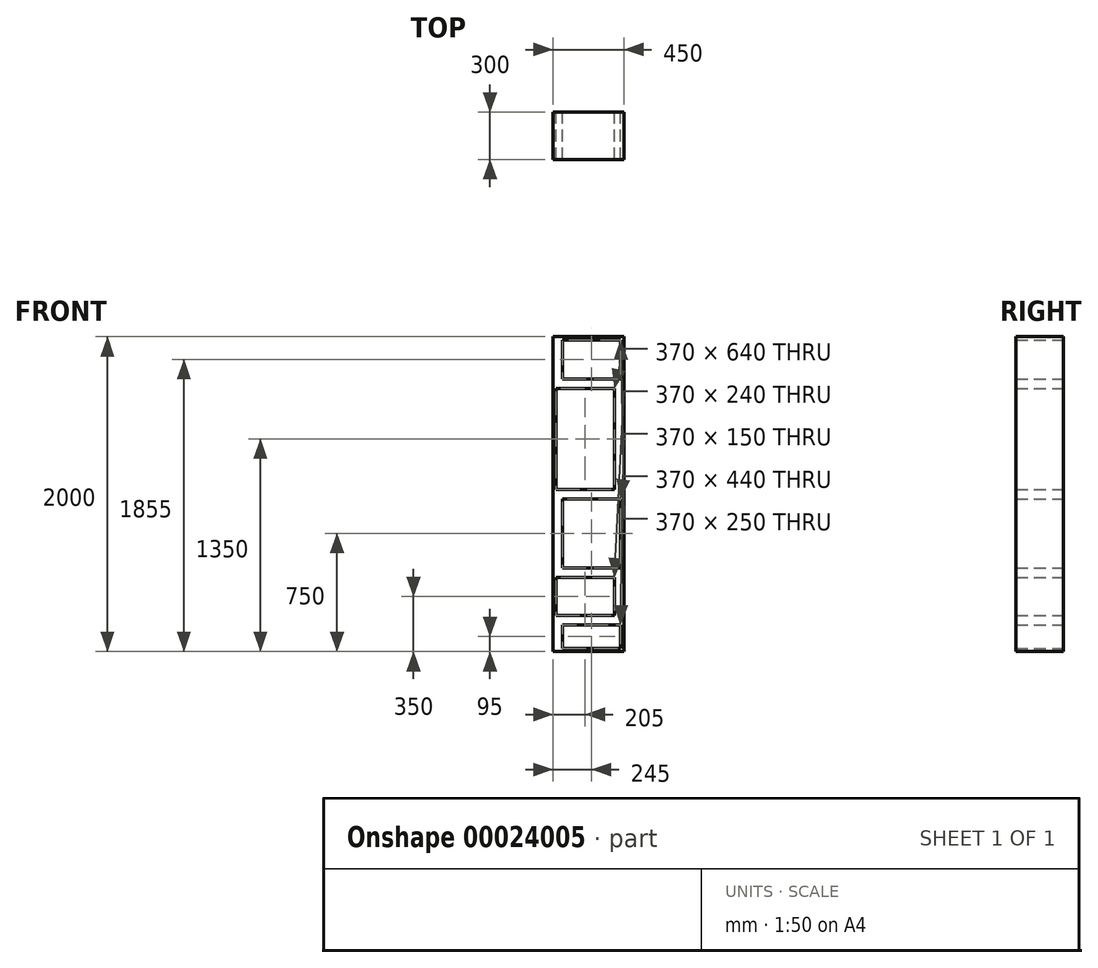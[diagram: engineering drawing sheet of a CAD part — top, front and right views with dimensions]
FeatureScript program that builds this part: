
annotation { "Feature Type Name" : "Feature", "Feature Type Description" : "" }
export const myFeature = defineFeature(function(context is Context, id is Id, definition is map)
    precondition{}
    {
        {
            var Q0;
            Q0=qCreatedBy(makeId("Front.planeOp"),FACE);
            var sketch = newSketch(context, id + "F0", { "sketchPlane" : qUnion([Q0])});
            skLineSegment(sketch, "E0.bottom", {"start": v(-1686.27, 784.55) * mm, "end": v(-1656.27, 784.55) * mm});
            skLineSegment(sketch, "E0.top", {"start": v(-1686.27, -1215.45) * mm, "end": v(-1656.27, -1215.45) * mm});
            skLineSegment(sketch, "E0.left", {"start": v(-1686.27, 784.55) * mm, "end": v(-1686.27, -215.45) * mm});
            skLineSegment(sketch, "E0.right", {"start": v(-1236.27, 784.55) * mm, "end": v(-1236.27, 484.55) * mm});
            skLineSegment(sketch, "E1.bottom", {"start": v(-1656.27, 784.55) * mm, "end": v(-1266.27, 784.55) * mm});
            skLineSegment(sketch, "E1.top", {"start": v(-1656.27, -1215.45) * mm, "end": v(-1266.27, -1215.45) * mm});
            skLineSegment(sketch, "E1.left", {"start": v(-1656.27, 784.55) * mm, "end": v(-1656.27, 484.55) * mm, "construction": true});
            skLineSegment(sketch, "E1.right", {"start": v(-1266.27, 784.55) * mm, "end": v(-1266.27, 484.55) * mm, "construction": true});
            skLineSegment(sketch, "E2.bottom", {"start": v(-1686.27, 484.55) * mm, "end": v(-1656.27, 484.55) * mm, "construction": true});
            skLineSegment(sketch, "E2.top", {"start": v(-1686.27, -215.45) * mm, "end": v(-1656.27, -215.45) * mm, "construction": true});
            skLineSegment(sketch, "E2.left", {"start": v(-1686.27, 484.55) * mm, "end": v(-1686.27, 484.55) * mm});
            skLineSegment(sketch, "E2.right", {"start": v(-1236.27, 484.55) * mm, "end": v(-1236.27, 484.55) * mm});
            skLineSegment(sketch, "E3.bottom", {"start": v(-1686.27, -715.45) * mm, "end": v(-1656.27, -715.45) * mm, "construction": true});
            skLineSegment(sketch, "E3.top", {"start": v(-1686.27, -1015.45) * mm, "end": v(-1656.27, -1015.45) * mm, "construction": true});
            skLineSegment(sketch, "E3.left", {"start": v(-1686.27, -715.45) * mm, "end": v(-1686.27, -715.45) * mm});
            skLineSegment(sketch, "E3.right", {"start": v(-1236.27, -715.45) * mm, "end": v(-1236.27, -715.45) * mm});
            skLineSegment(sketch, "E4", {"start": v(-1656.27, 484.55) * mm, "end": v(-1656.27, -215.45) * mm, "construction": true});
            skLineSegment(sketch, "E5", {"start": v(-1266.27, 484.55) * mm, "end": v(-1236.27, 484.55) * mm, "construction": true});
            skLineSegment(sketch, "E6", {"start": v(-1266.27, 484.55) * mm, "end": v(-1266.27, -215.45) * mm, "construction": true});
            skLineSegment(sketch, "E7", {"start": v(-1266.27, -215.45) * mm, "end": v(-1266.27, -715.45) * mm, "construction": true});
            skLineSegment(sketch, "E8", {"start": v(-1266.27, -715.45) * mm, "end": v(-1266.27, -1015.45) * mm, "construction": true});
            skLineSegment(sketch, "E9", {"start": v(-1266.27, -1015.45) * mm, "end": v(-1266.27, -1215.45) * mm, "construction": true});
            skLineSegment(sketch, "E10", {"start": v(-1656.27, -1015.45) * mm, "end": v(-1656.27, -1215.45) * mm, "construction": true});
            skLineSegment(sketch, "E11", {"start": v(-1656.27, -715.45) * mm, "end": v(-1656.27, -1015.45) * mm, "construction": true});
            skLineSegment(sketch, "E12", {"start": v(-1656.27, -215.45) * mm, "end": v(-1656.27, -715.45) * mm, "construction": true});
            skLineSegment(sketch, "E13", {"start": v(-1656.27, 484.55) * mm, "end": v(-1266.27, 484.55) * mm, "construction": true});
            skLineSegment(sketch, "E14", {"start": v(-1656.27, -215.45) * mm, "end": v(-1266.27, -215.45) * mm, "construction": true});
            skLineSegment(sketch, "E15", {"start": v(-1266.27, -215.45) * mm, "end": v(-1236.27, -215.45) * mm, "construction": true});
            skLineSegment(sketch, "E16", {"start": v(-1266.27, -715.45) * mm, "end": v(-1236.27, -715.45) * mm, "construction": true});
            skLineSegment(sketch, "E17", {"start": v(-1266.27, -1015.45) * mm, "end": v(-1236.27, -1015.45) * mm, "construction": true});
            skLineSegment(sketch, "E18", {"start": v(-1656.27, -1015.45) * mm, "end": v(-1266.27, -1015.45) * mm, "construction": true});
            skLineSegment(sketch, "E19", {"start": v(-1656.27, -715.45) * mm, "end": v(-1266.27, -715.45) * mm, "construction": true});
            skLineSegment(sketch, "E20", {"start": v(-1686.27, -1015.45) * mm, "end": v(-1686.27, -1215.45) * mm});
            skLineSegment(sketch, "E21", {"start": v(-1686.27, -715.45) * mm, "end": v(-1686.27, -1015.45) * mm});
            skLineSegment(sketch, "E22", {"start": v(-1686.27, -215.45) * mm, "end": v(-1686.27, -1015.45) * mm});
            skLineSegment(sketch, "E23", {"start": v(-1686.27, 484.55) * mm, "end": v(-1686.27, -215.45) * mm});
            skLineSegment(sketch, "E24", {"start": v(-1266.27, 784.55) * mm, "end": v(-1236.27, 784.55) * mm});
            skLineSegment(sketch, "E25", {"start": v(-1266.27, -1215.45) * mm, "end": v(-1236.27, -1215.45) * mm});
            skLineSegment(sketch, "E26", {"start": v(-1236.27, -1015.45) * mm, "end": v(-1236.27, -1215.45) * mm});
            skLineSegment(sketch, "E27", {"start": v(-1236.27, -715.45) * mm, "end": v(-1236.27, -1015.45) * mm});
            skLineSegment(sketch, "E28", {"start": v(-1236.27, -215.45) * mm, "end": v(-1236.27, -1015.45) * mm});
            skLineSegment(sketch, "E29", {"start": v(-1236.27, 484.55) * mm, "end": v(-1236.27, -215.45) * mm});
            skSolve(sketch);
        }
        {
            var Q0;
            Q0=qCreatedBy(makeId("Front.planeOp"),FACE);
            var sketch = newSketch(context, id + "F1", { "sketchPlane" : qUnion([Q0])});
            skLineSegment(sketch, "E30.0", {"start": v(-1646.27, -1025.45) * mm, "end": v(-1646.27, -1215.45) * mm});
            skLineSegment(sketch, "E30.1", {"start": v(-1646.27, -1025.45) * mm, "end": v(-1256.27, -1025.45) * mm});
            skLineSegment(sketch, "E30.2", {"start": v(-1256.27, -705.45) * mm, "end": v(-1256.27, -1025.45) * mm});
            skLineSegment(sketch, "E30.3", {"start": v(-1646.27, -705.45) * mm, "end": v(-1256.27, -705.45) * mm});
            skLineSegment(sketch, "E30.4", {"start": v(-1646.27, -225.45) * mm, "end": v(-1646.27, -705.45) * mm});
            skLineSegment(sketch, "E30.5", {"start": v(-1646.27, -225.45) * mm, "end": v(-1256.27, -225.45) * mm});
            skLineSegment(sketch, "E30.6", {"start": v(-1256.27, 494.55) * mm, "end": v(-1256.27, -225.45) * mm});
            skLineSegment(sketch, "E30.7", {"start": v(-1646.27, 494.55) * mm, "end": v(-1256.27, 494.55) * mm});
            skLineSegment(sketch, "E30.8", {"start": v(-1646.27, 784.55) * mm, "end": v(-1646.27, 494.55) * mm});
            skLineSegment(sketch, "E31.0", {"start": v(-1666.27, -1005.45) * mm, "end": v(-1666.27, -1215.45) * mm});
            skLineSegment(sketch, "E31.1", {"start": v(-1666.27, -1005.45) * mm, "end": v(-1276.27, -1005.45) * mm});
            skLineSegment(sketch, "E31.2", {"start": v(-1276.27, -725.45) * mm, "end": v(-1276.27, -1005.45) * mm});
            skLineSegment(sketch, "E31.3", {"start": v(-1666.27, -725.45) * mm, "end": v(-1276.27, -725.45) * mm});
            skLineSegment(sketch, "E31.4", {"start": v(-1666.27, -205.45) * mm, "end": v(-1666.27, -725.45) * mm});
            skLineSegment(sketch, "E31.5", {"start": v(-1666.27, -205.45) * mm, "end": v(-1276.27, -205.45) * mm});
            skLineSegment(sketch, "E31.6", {"start": v(-1276.27, 474.55) * mm, "end": v(-1276.27, -205.45) * mm});
            skLineSegment(sketch, "E31.7", {"start": v(-1666.27, 474.55) * mm, "end": v(-1276.27, 474.55) * mm});
            skLineSegment(sketch, "E31.8", {"start": v(-1666.27, 784.55) * mm, "end": v(-1666.27, 474.55) * mm});
            skLineSegment(sketch, "E32", {"start": v(-1646.27, -1215.45) * mm, "end": v(-1666.27, -1215.45) * mm});
            skLineSegment(sketch, "E33", {"start": v(-1666.27, 784.55) * mm, "end": v(-1646.27, 784.55) * mm});
            skSolve(sketch);
        }
        {
            var Q0;
            Q0=qCreatedBy(makeId("Front.planeOp"),FACE);
            var sketch = newSketch(context, id + "F2", { "sketchPlane" : qUnion([Q0])});
            skLineSegment(sketch, "E34.bottom", {"start": v(-1686.27, 474.55) * mm, "end": v(-1276.27, 474.55) * mm});
            skLineSegment(sketch, "E34.top", {"start": v(-1686.27, -205.45) * mm, "end": v(-1276.27, -205.45) * mm});
            skLineSegment(sketch, "E34.left", {"start": v(-1686.27, 474.55) * mm, "end": v(-1686.27, -205.45) * mm});
            skLineSegment(sketch, "E34.right", {"start": v(-1276.27, 474.55) * mm, "end": v(-1276.27, -205.45) * mm});
            skLineSegment(sketch, "E35.bottom", {"start": v(-1686.27, -725.45) * mm, "end": v(-1276.27, -725.45) * mm});
            skLineSegment(sketch, "E35.top", {"start": v(-1686.27, -1005.45) * mm, "end": v(-1276.27, -1005.45) * mm});
            skLineSegment(sketch, "E35.left", {"start": v(-1686.27, -725.45) * mm, "end": v(-1686.27, -1005.45) * mm});
            skLineSegment(sketch, "E35.right", {"start": v(-1276.27, -725.45) * mm, "end": v(-1276.27, -1005.45) * mm});
            skLineSegment(sketch, "E36.0", {"start": v(-1666.27, -745.45) * mm, "end": v(-1296.27, -745.45) * mm});
            skLineSegment(sketch, "E36.1", {"start": v(-1666.27, -745.45) * mm, "end": v(-1666.27, -985.45) * mm});
            skLineSegment(sketch, "E36.2", {"start": v(-1666.27, -985.45) * mm, "end": v(-1296.27, -985.45) * mm});
            skLineSegment(sketch, "E36.3", {"start": v(-1296.27, -745.45) * mm, "end": v(-1296.27, -985.45) * mm});
            skLineSegment(sketch, "E37.bottom", {"start": v(-1646.27, -1025.45) * mm, "end": v(-1236.27, -1025.45) * mm});
            skLineSegment(sketch, "E37.top", {"start": v(-1646.27, -1215.45) * mm, "end": v(-1236.27, -1215.45) * mm});
            skLineSegment(sketch, "E37.left", {"start": v(-1646.27, -1025.45) * mm, "end": v(-1646.27, -1215.45) * mm});
            skLineSegment(sketch, "E37.right", {"start": v(-1236.27, -1025.45) * mm, "end": v(-1236.27, -1215.45) * mm});
            skLineSegment(sketch, "E38.bottom", {"start": v(-1646.27, -225.45) * mm, "end": v(-1236.27, -225.45) * mm});
            skLineSegment(sketch, "E38.top", {"start": v(-1646.27, -705.45) * mm, "end": v(-1236.27, -705.45) * mm});
            skLineSegment(sketch, "E38.left", {"start": v(-1646.27, -225.45) * mm, "end": v(-1646.27, -705.45) * mm});
            skLineSegment(sketch, "E38.right", {"start": v(-1236.27, -225.45) * mm, "end": v(-1236.27, -705.45) * mm});
            skLineSegment(sketch, "E39.bottom", {"start": v(-1646.27, 494.55) * mm, "end": v(-1236.27, 494.55) * mm});
            skLineSegment(sketch, "E39.top", {"start": v(-1646.27, 784.55) * mm, "end": v(-1236.27, 784.55) * mm});
            skLineSegment(sketch, "E39.left", {"start": v(-1646.27, 494.55) * mm, "end": v(-1646.27, 784.55) * mm});
            skLineSegment(sketch, "E39.right", {"start": v(-1236.27, 494.55) * mm, "end": v(-1236.27, 784.55) * mm});
            skLineSegment(sketch, "E40.0", {"start": v(-1626.27, -245.45) * mm, "end": v(-1256.27, -245.45) * mm});
            skLineSegment(sketch, "E40.1", {"start": v(-1626.27, -245.45) * mm, "end": v(-1626.27, -685.45) * mm});
            skLineSegment(sketch, "E40.2", {"start": v(-1626.27, -685.45) * mm, "end": v(-1256.27, -685.45) * mm});
            skLineSegment(sketch, "E40.3", {"start": v(-1256.27, -245.45) * mm, "end": v(-1256.27, -685.45) * mm});
            skLineSegment(sketch, "E41.0", {"start": v(-1666.27, 454.55) * mm, "end": v(-1666.27, -185.45) * mm});
            skLineSegment(sketch, "E41.1", {"start": v(-1666.27, 454.55) * mm, "end": v(-1296.27, 454.55) * mm});
            skLineSegment(sketch, "E41.2", {"start": v(-1296.27, 454.55) * mm, "end": v(-1296.27, -185.45) * mm});
            skLineSegment(sketch, "E41.3", {"start": v(-1666.27, -185.45) * mm, "end": v(-1296.27, -185.45) * mm});
            skLineSegment(sketch, "E42.0", {"start": v(-1626.27, -1045.45) * mm, "end": v(-1626.27, -1195.45) * mm});
            skLineSegment(sketch, "E42.1", {"start": v(-1626.27, -1045.45) * mm, "end": v(-1256.27, -1045.45) * mm});
            skLineSegment(sketch, "E42.2", {"start": v(-1256.27, -1045.45) * mm, "end": v(-1256.27, -1195.45) * mm});
            skLineSegment(sketch, "E42.3", {"start": v(-1626.27, -1195.45) * mm, "end": v(-1256.27, -1195.45) * mm});
            skLineSegment(sketch, "E43.0", {"start": v(-1256.27, 514.55) * mm, "end": v(-1256.27, 764.55) * mm});
            skLineSegment(sketch, "E43.1", {"start": v(-1626.27, 514.55) * mm, "end": v(-1256.27, 514.55) * mm});
            skLineSegment(sketch, "E43.2", {"start": v(-1626.27, 514.55) * mm, "end": v(-1626.27, 764.55) * mm});
            skLineSegment(sketch, "E43.3", {"start": v(-1626.27, 764.55) * mm, "end": v(-1256.27, 764.55) * mm});
            skSolve(sketch);
        }
        {
            var Q0;
            Q0=qCreatedBy(makeId("Front.planeOp"),FACE);
            var sketch = newSketch(context, id + "F3", { "sketchPlane" : qUnion([Q0])});
            skLineSegment(sketch, "E44.bottom", {"start": v(-1686.27, 784.55) * mm, "end": v(-1236.27, 784.55) * mm, "construction": true});
            skLineSegment(sketch, "E44.top", {"start": v(-1686.27, -1215.45) * mm, "end": v(-1236.27, -1215.45) * mm, "construction": true});
            skLineSegment(sketch, "E44.left", {"start": v(-1686.27, 784.55) * mm, "end": v(-1686.27, -1215.45) * mm});
            skLineSegment(sketch, "E44.right", {"start": v(-1236.27, 784.55) * mm, "end": v(-1236.27, -1215.45) * mm});
            skLineSegment(sketch, "E45.0", {"start": v(-1666.27, 784.55) * mm, "end": v(-1666.27, -1215.45) * mm});
            skLineSegment(sketch, "E46.0", {"start": v(-1256.27, 784.55) * mm, "end": v(-1256.27, -1215.45) * mm});
            skLineSegment(sketch, "E47.bottom", {"start": v(-1686.27, 784.55) * mm, "end": v(-1666.27, 784.55) * mm});
            skLineSegment(sketch, "E47.top", {"start": v(-1686.27, -1215.45) * mm, "end": v(-1666.27, -1215.45) * mm});
            skLineSegment(sketch, "E48.bottom", {"start": v(-1256.27, 784.55) * mm, "end": v(-1236.27, 784.55) * mm});
            skLineSegment(sketch, "E48.top", {"start": v(-1256.27, -1215.45) * mm, "end": v(-1236.27, -1215.45) * mm});
            skSolve(sketch);
        }
        {
            var Q0;
            Q0=makeQuery(id+"F1.imprint","IMPRINT",FACE,{"disambiguationData":[TD([[makeQuery(id+"F1.imprint","IMPRINT",EDGE,{"derivedFrom":sQuery(id+"F1.wireOp",EDGE,"E30.0")}),-1.0]])]});
            extrude(context, id + "F4", {"entities" : qUnion([Q0]), "depth" : 300 * mm});
        }
        {
            var Q0;
            Q0=makeQuery(id+"F2.imprint","IMPRINT",FACE,{"disambiguationData":[TD([[makeQuery(id+"F2.imprint","IMPRINT",EDGE,{"derivedFrom":sQuery(id+"F2.wireOp",EDGE,"E39.bottom")}),1.0]])]});
            var Q1;
            Q1=makeQuery(id+"F2.imprint","IMPRINT",FACE,{"disambiguationData":[TD([[makeQuery(id+"F2.imprint","IMPRINT",EDGE,{"derivedFrom":sQuery(id+"F2.wireOp",EDGE,"E38.bottom")}),-1.0]])]});
            var Q2;
            Q2=makeQuery(id+"F2.imprint","IMPRINT",FACE,{"disambiguationData":[TD([[makeQuery(id+"F2.imprint","IMPRINT",EDGE,{"derivedFrom":sQuery(id+"F2.wireOp",EDGE,"E37.bottom")}),-1.0]])]});
            var Q3;
            Q3=makeQuery(id+"F2.imprint","IMPRINT",FACE,{"disambiguationData":[TD([[makeQuery(id+"F2.imprint","IMPRINT",EDGE,{"derivedFrom":sQuery(id+"F2.wireOp",EDGE,"E35.bottom")}),-1.0]])]});
            var Q4;
            Q4=makeQuery(id+"F2.imprint","IMPRINT",FACE,{"disambiguationData":[TD([[makeQuery(id+"F2.imprint","IMPRINT",EDGE,{"derivedFrom":sQuery(id+"F2.wireOp",EDGE,"E34.bottom")}),-1.0]])]});
            extrude(context, id + "F5", {"entities" : qUnion([Q0, Q1, Q2, Q3, Q4]), "depth" : 300 * mm});
        }
        {
            var Q0;
            Q0=makeQuery(id+"F3.imprint","IMPRINT",FACE,{"disambiguationData":[TD([[makeQuery(id+"F3.imprint","IMPRINT",EDGE,{"derivedFrom":sQuery(id+"F3.wireOp",EDGE,"E47.bottom")}),-1.0]])]});
            extrude(context, id + "F6", {"entities" : qUnion([Q0]), "operationType" : NewBodyOperationType.ADD, "depth" : 300 * mm});
        }
        {
            var Q0;
            Q0=makeQuery(id+"F3.imprint","IMPRINT",FACE,{"disambiguationData":[TD([[makeQuery(id+"F3.imprint","IMPRINT",EDGE,{"derivedFrom":sQuery(id+"F3.wireOp",EDGE,"E48.bottom")}),-1.0]])]});
            extrude(context, id + "F7", {"entities" : qUnion([Q0]), "operationType" : NewBodyOperationType.ADD, "depth" : 300 * mm});
        }
    });
